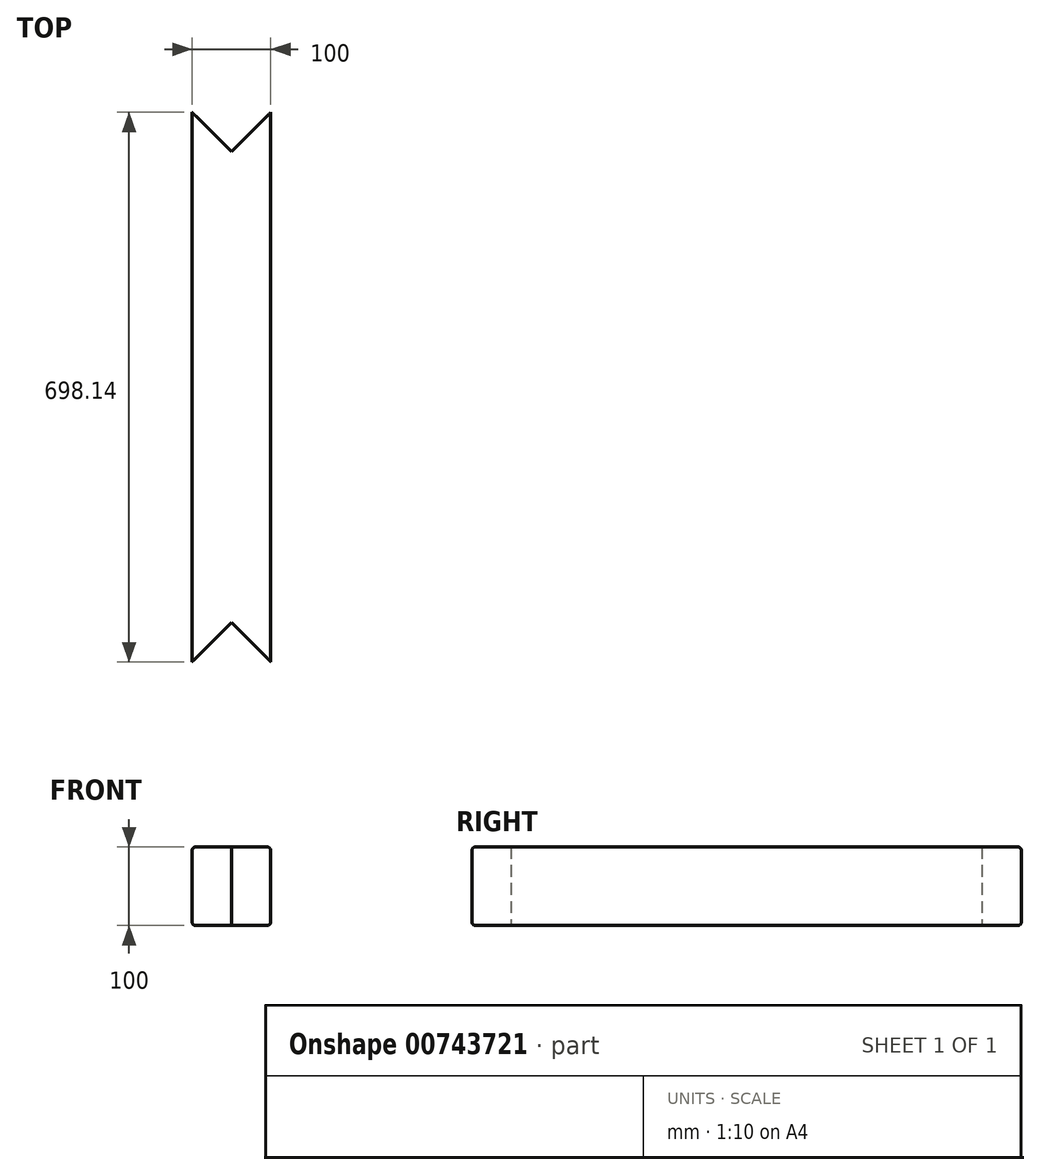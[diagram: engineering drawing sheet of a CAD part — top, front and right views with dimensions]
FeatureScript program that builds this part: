
annotation { "Feature Type Name" : "Feature", "Feature Type Description" : "" }
export const myFeature = defineFeature(function(context is Context, id is Id, definition is map)
    precondition{}
    {
        {
            var Q0;
            Q0=qCreatedBy(makeId("Top.planeOp"),FACE);
            var sketch = newSketch(context, id + "F0", { "sketchPlane" : qUnion([Q0])});
            skLineSegment(sketch, "E0.left", {"start": v(-50, -349.07) * mm, "end": v(-50, 349.07) * mm});
            skLineSegment(sketch, "E0.right", {"start": v(50, -349.07) * mm, "end": v(50, 349.07) * mm});
            skPoint(sketch, "E0.middle", {"position": v(0, 0) * mm});
            skLineSegment(sketch, "E1", {"start": v(50, 349.07) * mm, "end": v(0, 299.07) * mm});
            skLineSegment(sketch, "E2", {"start": v(0, 299.07) * mm, "end": v(-50, 349.07) * mm});
            skLineSegment(sketch, "E3", {"start": v(50, -349.07) * mm, "end": v(0, -299.07) * mm});
            skLineSegment(sketch, "E4", {"start": v(0, -299.07) * mm, "end": v(-50, -349.07) * mm});
            skSolve(sketch);
        }
        {
            var Q0;
            Q0 = qSketchRegion(id + "F0", true);
            extrude(context, id + "F1", {"entities" : qUnion([Q0]), "depth" : 100 * mm, "offsetDistance" : 25 * mm});
        }
        {
            var Q0;
            Q0=makeQuery(id+"F1.opExtrude","CAP_EDGE",EDGE,{"disambiguationData":[OSD([sQuery(id+"F0.wireOp",EDGE,"E0.right")])],"isStart":false});
            var Q1;
            Q1=makeQuery(id+"F1.opExtrude","CAP_EDGE",EDGE,{"disambiguationData":[OSD([sQuery(id+"F0.wireOp",EDGE,"E0.right")])],"isStart":true});
            var Q2;
            Q2=makeQuery(id+"F1.opExtrude","CAP_EDGE",EDGE,{"disambiguationData":[OSD([sQuery(id+"F0.wireOp",EDGE,"E0.left")])],"isStart":false});
            var Q3;
            Q3=makeQuery(id+"F1.opExtrude","CAP_EDGE",EDGE,{"disambiguationData":[OSD([sQuery(id+"F0.wireOp",EDGE,"E0.left")])],"isStart":true});
            fillet(context, id + "F2", {"entities" : qUnion([Q0, Q1, Q2, Q3]), "radius" : 5 * mm, "tangentPropagation" : true, "allowEdgeOverflow" : false});
        }
    });
